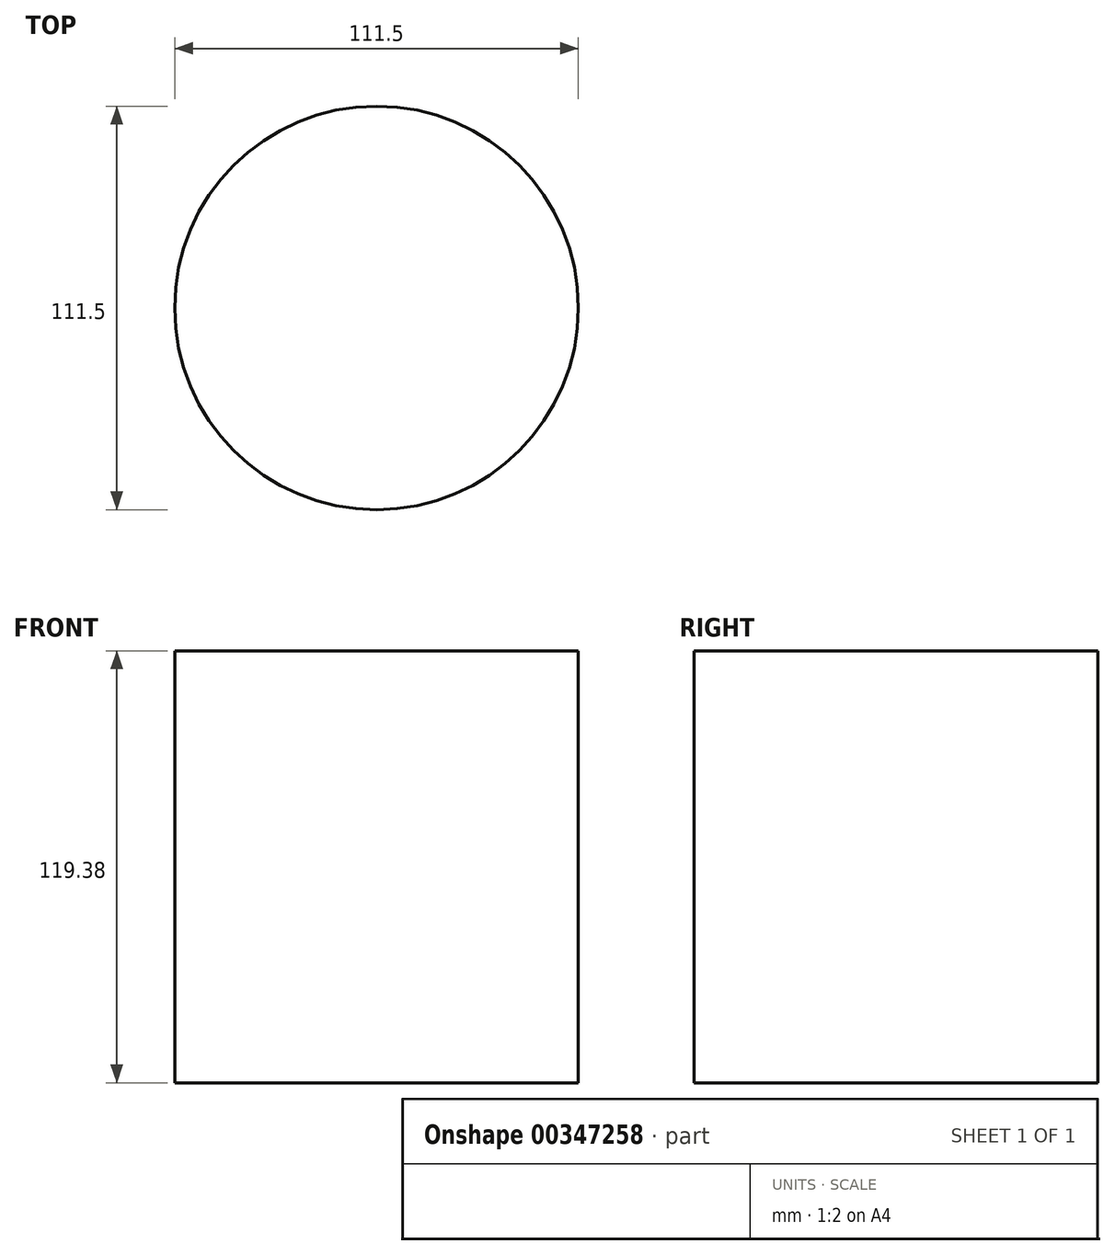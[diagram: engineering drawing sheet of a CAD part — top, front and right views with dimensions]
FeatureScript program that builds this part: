
annotation { "Feature Type Name" : "Feature", "Feature Type Description" : "" }
export const myFeature = defineFeature(function(context is Context, id is Id, definition is map)
    precondition{}
    {
        {
            var Q0;
            Q0=qCreatedBy(makeId("Top.planeOp"),FACE);
            var sketch = newSketch(context, id + "F0", { "sketchPlane" : qUnion([Q0])});
            skCircle(sketch, "E0", {"center": v(0, 0) * mm, "radius": 55.75 * mm});
            skSolve(sketch);
        }
        {
            var Q0;
            Q0=makeQuery(id+"F0.imprint","IMPRINT",FACE,{"disambiguationData":[TD([[makeQuery(id+"F0.imprint","IMPRINT",EDGE,{"derivedFrom":sQuery(id+"F0.wireOp",EDGE,"E0")}),1.0]])]});
            extrude(context, id + "F1", {"entities" : qUnion([Q0]), "oppositeDirection" : true, "depth" : 119.38 * mm});
        }
    });
